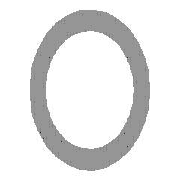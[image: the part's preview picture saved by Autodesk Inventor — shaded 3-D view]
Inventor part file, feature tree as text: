
AUTODESK INVENTOR PART (.ipt)
format: ipt  version: 2021 (Build 250183000, 183)  size: 333,824 bytes
history: native  units: mm (DEFAULTED — no unit token found)
features: other x5, plane x2, sketch x2, sweep x1
ambient origin geometry x8: Origin, YZ Plane, XZ Plane, XY Plane, X Axis, Y Axis, Z Axis, Center Point
bodies: Solid1 (feature_tree)
feature tree (10):
  parser-record x1  (decoder bookkeeping rows leaked as tree rows — omitted from the tree; the rows remain in map.json)
  other  "Driven Length"
  other  "Plano inicial"
  other  "Plano final"
  other  "Trayectoria de barrido"
  plane  "Plano de trabajo de orientación"
  sweep  "Cuerpo"
  sketch  "Sketch3"  dims[d0=21.336mm d1=2.7686mm]
  plane  "Work Plane3"
  sketch  "Sketch4"  dims[d4=-0.0mm d5=1183.592627mm d6=90.0deg d7=1183.592627mm d8=0.0mm d9=0.0mm]
